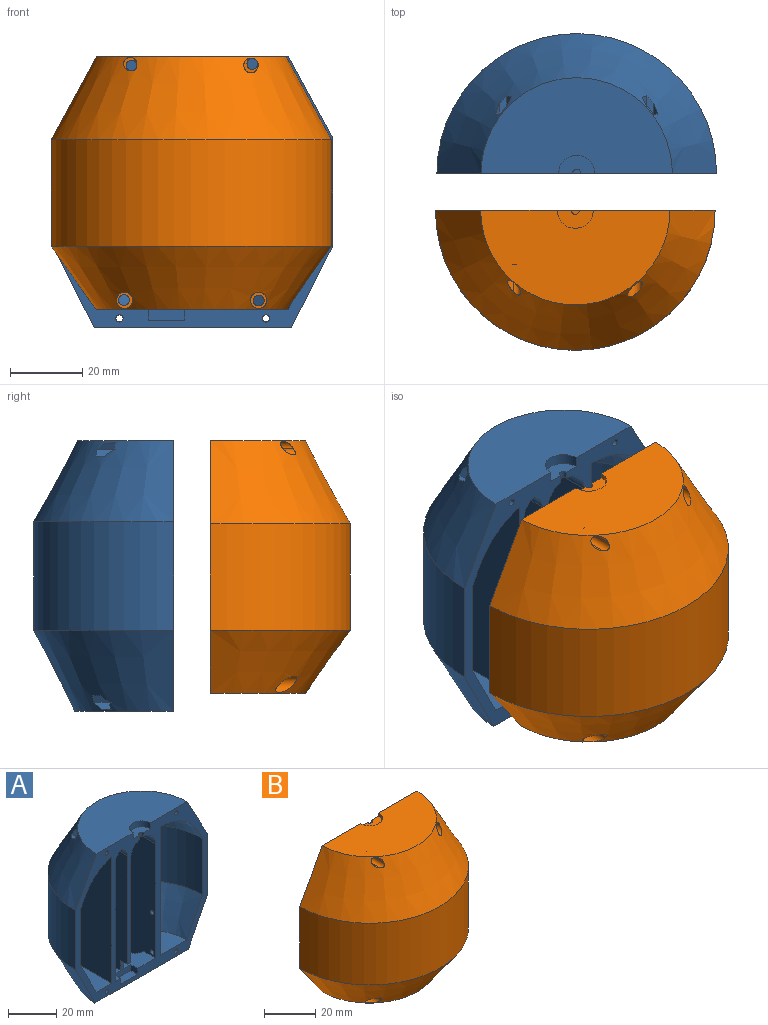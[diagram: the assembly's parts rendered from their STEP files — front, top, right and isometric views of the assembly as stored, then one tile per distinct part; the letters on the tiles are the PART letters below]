
ASSEMBLY  parts=2 mates=2
PART A: 77 faces, bbox 80.7x42x78.3 mm
  f0: cone r=27.29mm half-angle=26.9deg, axis (0,0,1), area 2579.3mm2, adj f10,f12,f15,f49,f50,f51,f52,f53
  f1: cone r=38.71mm half-angle=28.6deg, axis (0,0,-1), area 2584.5mm2, adj f2,f10,f15,f63,f64,f65,f66,f67
  f2: plane 52.93x26.47mm, normal (0,0,1), area 1061mm2, adj f1,f10,f37
  f3: cylinder r=1.12mm len=2.28mm, axis (0,0,1), area 7.4mm2, adj f8,f10,f36,f41,f43
  f4: plane 28.49x26.47mm, normal (0,0,1), area 362.5mm2, adj f10,f13,f16,f21,f24,f26,f28,f29
  f5: plane 24x15.31mm, normal (0,0,1), area 263.9mm2, adj f10,f13,f27
  f6: cone r=25.77mm half-angle=28.6deg, axis (0,0,-1), area 701mm2, adj f10,f14,f38
  f7: plane 2.84x0.35mm, normal (0,0,-1), area 0.7mm2, adj f10,f27,f38
  f8: plane 10.91x0.09mm, normal (0,0,-1), area 1mm2, adj f3,f38,f41,f43
  f9: plane 18x7mm, normal (0,0,1), area 110mm2, adj f10,f18,f19,f20,f22,f26
  f10: plane 77.43x75mm, normal (0,-1,0), area 1447.8mm2, adj f0,f1,f2,f3,f4,f5,f6,f7
  f11: plane 20x9.13mm, normal (0,0,1), area 126.7mm2, adj f10,f13,f17
  f12: plane 54.59x27.29mm, normal (0,0,-1), area 1130.8mm2, adj f0,f10,f29,f30
  f13: cone r=26.47mm half-angle=26.9deg, axis (0,0,1), area 1995.5mm2, adj f4,f5,f10,f11,f14
  f14: cylinder r=35.71mm len=71.43mm, axis (0,0,1), area 3199.8mm2, adj f6,f10,f13
  f15: cylinder r=38.71mm len=77.43mm, axis (0,0,1), area 3648.7mm2, adj f0,f1,f10
  f16: plane 65.51x20.38mm, normal (0,1,0), area 690.7mm2, adj f4,f17,f21,f38,f42
  f17: plane 64.28x20mm, normal (-1,0,0), area 1259.6mm2, adj f10,f11,f16,f38
  f18: plane 60x18mm, normal (1,0,0), area 1080mm2, adj f9,f10,f19,f39
  f19: plane 64.77x7mm, normal (0,-1,0), area 444.5mm2, adj f9,f18,f20,f39,f40
  f20: plane 60x18mm, normal (-1,0,0), area 1060mm2, adj f9,f10,f19,f25,f26,f40
  f21: plane 57.8x20mm, normal (1,0,0), area 1129.6mm2, adj f4,f10,f16,f25,f26,f41,f42
  f22: plane 4x3mm, normal (1,0,0), area 12mm2, adj f9,f10,f23,f26
  f23: plane 10x4mm, normal (0,0,1), area 40mm2, adj f10,f22,f24,f26
  f24: plane 4x3mm, normal (-1,0,0), area 12mm2, adj f4,f10,f23,f26
  f25: plane 4x2mm, normal (0,0,-1), area 8mm2, adj f10,f20,f21,f26
  f26: plane 10x8mm, normal (0,-1,0), area 40mm2, adj f4,f9,f20,f21,f22,f23,f24,f25
  f27: plane 65.74x24.74mm, normal (1,0,0), area 1499mm2, adj f5,f7,f10,f28,f31,f32,f33,f34
  f28: plane 64.74x17.31mm, normal (0,1,0), area 204.1mm2, adj f4,f27,f29,f35,f38,f44
  f29: plane 62.8x24mm, normal (-1,0,0), area 1403.1mm2, adj f4,f10,f12,f28,f30,f31,f32,f33
  f30: cylinder r=5mm len=10mm, axis (0,0,1), area 78.5mm2, adj f4,f12,f29
  f31: cylinder r=1mm len=3mm, axis (-1,0,0), area 18.8mm2, adj f27,f29
  f32: cylinder r=1mm len=3mm, axis (-1,0,0), area 18.8mm2, adj f27,f29
  f33: cylinder r=1mm len=3mm, axis (-1,0,0), area 18.8mm2, adj f27,f29
  f34: cylinder r=1mm len=3mm, axis (-1,0,0), area 18.8mm2, adj f27,f29
  f35: bspline ~14.04x10.94mm, area 26.3mm2, adj f27,f28,f38
  f36: plane 10x5mm, normal (0,0,1), area 37.3mm2, adj f3,f10,f37
  f37: cylinder r=5mm len=10mm, axis (0,0,1), area 47.1mm2, adj f2,f10,f36
  f38: torus R=11.51mm, axis (0,0,-1), area 1436.6mm2, adj f6,f7,f8,f10,f16,f17,f27,f28
  f39: cylinder r=5mm len=18mm, axis (0,1,0), area 113.9mm2, adj f10,f18,f19,f40
  f40: cylinder r=5mm len=18mm, axis (0,-1,0), area 113.9mm2, adj f10,f19,f20,f39
  f41: cylinder r=7.2mm len=11.48mm, axis (0,1,0), area 129.1mm2, adj f3,f8,f10,f21,f42
  f42: bspline ~16.88x10.33mm, area 107.9mm2, adj f16,f21,f38,f41
  f43: cylinder r=7.2mm len=11.47mm, axis (0,-1,0), area 129.7mm2, adj f3,f8,f10,f29,f44
  f44: bspline ~19.13x13.22mm, area 164mm2, adj f28,f29,f38,f43
  f45: cylinder r=1mm len=15mm, axis (0,-1,0), area 94.2mm2, adj f10,f76
  f46: cylinder r=1mm len=15mm, axis (0,-1,0), area 94.2mm2, adj f10,f69
  f47: cylinder r=1mm len=15mm, axis (0,-1,0), area 94.2mm2, adj f10,f62
  f48: cylinder r=1mm len=15mm, axis (0,-1,0), area 94.2mm2, adj f10,f55
  f49: plane 7.12x1.92mm, normal (-0.87,0,0.5), area 12.8mm2, adj f0,f50,f54,f55
  f50: plane 7.39x1.86mm, normal (-0.86,0,-0.5), area 15.5mm2, adj f0,f49,f51,f55
  f51: plane 7.38x2.14mm, normal (0,0,-1), area 13.7mm2, adj f0,f50,f52,f55
  f52: plane 5.41x1.94mm, normal (0.87,0,-0.5), area 8.6mm2, adj f0,f51,f53,f55
  f53: plane 2.67x1.86mm, normal (0.86,0,0.5), area 5.6mm2, adj f0,f52,f54,f55
  f54: plane 4.85x2.14mm, normal (0,0,1), area 8mm2, adj f0,f49,f53,f55
  f55: plane 4.29x3.72mm, normal (0,1,0), area 8.8mm2, adj f48,f49,f50,f51,f52,f53,f54
  f56: plane 2.95x1.88mm, normal (-0.91,0,0.42), area 5.6mm2, adj f0,f57,f61,f62
  f57: plane 5.65x1.75mm, normal (-0.82,0,-0.58), area 8.9mm2, adj f0,f56,f58,f62
  f58: plane 7.38x2.06mm, normal (0.09,0,-1), area 13.4mm2, adj f0,f57,f59,f62
  f59: plane 7.38x1.88mm, normal (0.91,0,-0.42), area 14.7mm2, adj f0,f58,f60,f62
  f60: plane 6.91x1.74mm, normal (0.82,0,0.58), area 11.9mm2, adj f0,f59,f61,f62
  f61: plane 4.62x2.06mm, normal (-0.09,0,1), area 7.4mm2, adj f0,f56,f60,f62
  f62: plane 4.11x3.75mm, normal (0,1,0), area 7.9mm2, adj f47,f56,f57,f58,f59,f60,f61
  f63: plane 4.46x1.88mm, normal (-0.86,0,0.51), area 6.3mm2, adj f1,f64,f68,f69
  f64: plane 1.82x1.56mm, normal (-0.87,0,-0.49), area 3mm2, adj f1,f63,f65,f69
  f65: plane 3.69x2.09mm, normal (-0.01,0,-1), area 5.3mm2, adj f1,f64,f66,f69
  f66: plane 6.1x1.86mm, normal (0.86,0,-0.51), area 10.2mm2, adj f1,f65,f67,f69
  f67: plane 6.45x1.82mm, normal (0.87,0,0.49), area 13mm2, adj f1,f66,f68,f69
  f68: plane 6.44x2.09mm, normal (0.01,0,1), area 11.4mm2, adj f1,f63,f67,f69
  f69: plane 4.17x3.63mm, normal (0,1,0), area 8.2mm2, adj f46,f63,f64,f65,f66,f67,f68
  f70: plane 6.43x1.79mm, normal (-0.84,0,0.54), area 13.3mm2, adj f1,f71,f75,f76
  f71: plane 6.19x1.94mm, normal (-0.89,0,-0.46), area 10.6mm2, adj f1,f70,f72,f76
  f72: plane 3.83x2.11mm, normal (-0.04,0,-1), area 5.5mm2, adj f1,f71,f73,f76
  f73: plane 1.79x1.43mm, normal (0.84,0,-0.54), area 2.9mm2, adj f1,f72,f74,f76
  f74: plane 4.33x1.96mm, normal (0.89,0,0.46), area 6.1mm2, adj f1,f73,f75,f76
  f75: plane 6.43x2.11mm, normal (0.04,0,1), area 11.3mm2, adj f1,f70,f74,f76
  f76: plane 4.22x3.75mm, normal (0,1,0), area 8.4mm2, adj f45,f70,f71,f72,f73,f74,f75
PART B: 41 faces, bbox 77.4x38.7x70 mm
  f0: plane 43.13x26.2mm, normal (0,0,1), area 713.5mm2, adj f1,f2,f17,f32,f36,f40
  f1: plane 77.43x70mm, normal (0,1,0), area 1098.6mm2, adj f0,f2,f3,f4,f5,f6,f7,f8
  f2: plane 60x20mm, normal (1,0,0), area 1180mm2, adj f0,f1,f19,f32,f39,f40
  f3: plane 60x18mm, normal (-1,0,0), area 1060mm2, adj f1,f6,f16,f34,f39,f40
  f4: plane 20x9.27mm, normal (0,0,1), area 128.8mm2, adj f1,f17,f33
  f5: cone r=25.51mm half-angle=28.6deg, axis (0,0,-1), area 2051.9mm2, adj f1,f7,f18,f19,f32,f33
  f6: plane 18x7mm, normal (0,0,-1), area 126mm2, adj f1,f3,f34,f35
  f7: plane 19.08x8.58mm, normal (0,0,-1), area 113.5mm2, adj f1,f5,f33
  f8: cone r=26.33mm half-angle=35.4deg, axis (0,0,1), area 2131mm2, adj f1,f15,f20,f24,f26
  f9: cone r=38.71mm half-angle=28.6deg, axis (0,0,-1), area 2634.2mm2, adj f1,f10,f11,f14,f20,f28,f30
  f10: cylinder r=1.5mm len=20mm, axis (0,1,0), area 147.3mm2, adj f1,f9,f30,f31
  f11: cylinder r=1.5mm len=23.48mm, axis (0,1,0), area 166.5mm2, adj f1,f9,f28,f29
  f12: cylinder r=1.5mm len=15mm, axis (0,1,0), area 141.4mm2, adj f1,f27
  f13: cylinder r=1.5mm len=15mm, axis (0,1,0), area 141.4mm2, adj f1,f25
  f14: plane 52.4x26.2mm, normal (0,0,1), area 1039.1mm2, adj f1,f9,f22
  f15: plane 52.66x26.33mm, normal (0,0,-1), area 1088.8mm2, adj f1,f8
  f16: plane 18x7mm, normal (0,0,1), area 110mm2, adj f1,f3,f34,f35,f38,f40
  f17: cone r=26.2mm half-angle=35.4deg, axis (0,0,1), area 1596.4mm2, adj f0,f1,f4,f18
  f18: cylinder r=35.71mm len=71.43mm, axis (0,0,1), area 3127.4mm2, adj f1,f5,f17
  f19: plane 41.34x25.51mm, normal (0,0,-1), area 687.1mm2, adj f1,f2,f5,f21,f32
  f20: cylinder r=38.71mm len=77.43mm, axis (0,0,1), area 3599.4mm2, adj f1,f8,f9
  f21: cylinder r=1.12mm len=3.5mm, axis (0,0,1), area 12.3mm2, adj f1,f19,f23
  f22: cylinder r=5mm len=10mm, axis (0,0,1), area 23.6mm2, adj f1,f14,f23
  f23: plane 10x5mm, normal (0,0,1), area 37.3mm2, adj f1,f21,f22
  f24: cylinder r=2.25mm len=8.76mm, axis (0,1,0), area 83.3mm2, adj f8,f25
  f25: plane 4.5x4.5mm, normal (0,-1,0), area 8.8mm2, adj f13,f24
  f26: cylinder r=2.25mm len=8.9mm, axis (0,1,0), area 85.8mm2, adj f8,f27
  f27: plane 4.5x4.5mm, normal (0,-1,0), area 8.8mm2, adj f12,f26
  f28: cylinder r=1.84mm len=7.97mm, axis (0,1,0), area 51.3mm2, adj f9,f11,f29
  f29: plane 3.69x3.68mm, normal (0,-1,0), area 4mm2, adj f11,f28
  f30: cylinder r=2.03mm len=8.95mm, axis (0,1,0), area 82.3mm2, adj f9,f10,f31
  f31: plane 4.05x4.05mm, normal (0,-1,0), area 5.8mm2, adj f10,f30
  f32: plane 60.02x11.02mm, normal (0,-1,0), area 659.5mm2, adj f0,f2,f5,f19,f33
  f33: plane 60.01x20.01mm, normal (-1,0,0), area 1199.4mm2, adj f1,f4,f5,f7,f32
  f34: plane 60x7mm, normal (0,1,0), area 420mm2, adj f3,f6,f16,f35
  f35: plane 60x18mm, normal (1,0,0), area 1080mm2, adj f1,f6,f16,f34
  f36: plane 4x3mm, normal (-1,0,0), area 12mm2, adj f0,f1,f37,f40
  f37: plane 10x4mm, normal (0,0,1), area 40mm2, adj f1,f36,f38,f40
  f38: plane 4x3mm, normal (1,0,0), area 12mm2, adj f1,f16,f37,f40
  f39: plane 4x2mm, normal (0,0,-1), area 8mm2, adj f1,f2,f3,f40
  f40: plane 10x8mm, normal (0,1,0), area 40mm2, adj f0,f2,f3,f16,f36,f37,f38,f39
PLACE A t=(-86.74,18.69,-56.92)mm
PLACE B t=(-87.14,8.46,-54.42)mm
MATE planar B.f14 <-> A.f2  axis (0,0,1) through (-87.14,-3,-19.42)mm
MATE planar A.f17 <-> B.f33  axis (-1,0,0) through (-104.07,28.58,-57.92)mm
